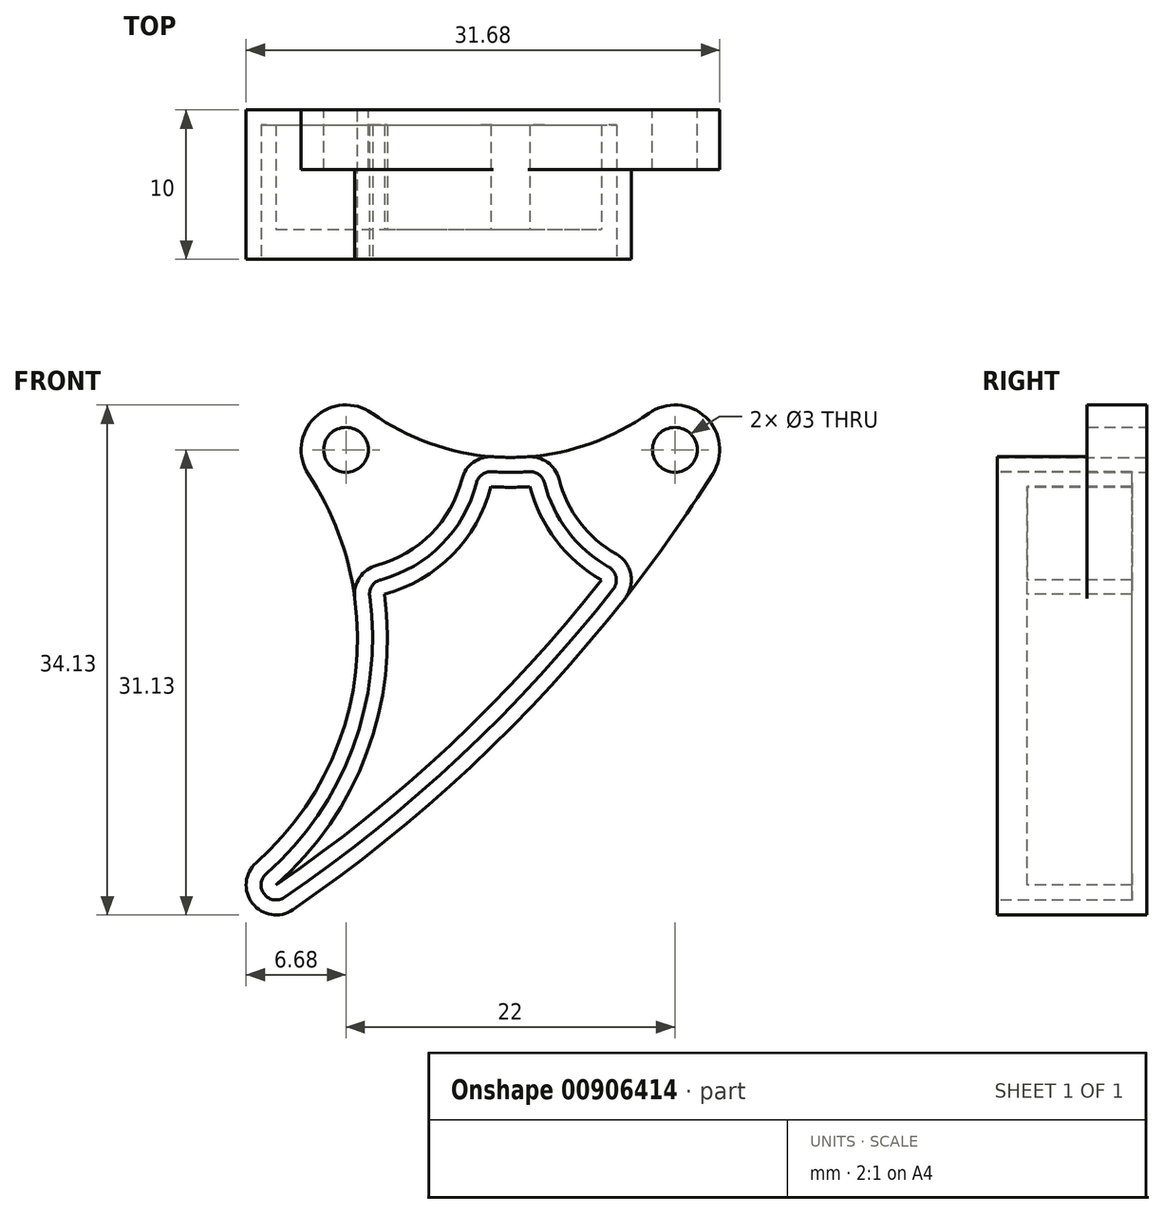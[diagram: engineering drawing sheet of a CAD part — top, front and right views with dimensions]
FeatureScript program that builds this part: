
annotation { "Feature Type Name" : "Feature", "Feature Type Description" : "" }
export const myFeature = defineFeature(function(context is Context, id is Id, definition is map)
    precondition{}
    {
        {
            var Q0;
            Q0=qCreatedBy(makeId("Front.planeOp"),FACE);
            var sketch = newSketch(context, id + "F0", { "sketchPlane" : qUnion([Q0])});
            skArc(sketch, "E0", {"start": v(1.74, 2.45) * mm, "mid": v(-2.08, 2.16) * mm, "end": v(-2.5, -1.65) * mm});
            skArc(sketch, "E1", {"start": v(24.54, -1.6) * mm, "mid": v(24.06, 2.18) * mm, "end": v(20.26, 2.45) * mm});
            skArc(sketch, "E2", {"start": v(1.74, 2.45) * mm, "mid": v(11, -0.5) * mm, "end": v(20.26, 2.45) * mm});
            skArc(sketch, "E3", {"start": v(-6, -27.63) * mm, "mid": v(0.6, -15.29) * mm, "end": v(-2.5, -1.65) * mm});
            skArc(sketch, "E4", {"start": v(-6, -27.63) * mm, "mid": v(-6.26, -30.35) * mm, "end": v(-3.55, -30.78) * mm});
            skArc(sketch, "E5", {"start": v(-3.55, -30.78) * mm, "mid": v(11.99, -17.62) * mm, "end": v(24.54, -1.6) * mm});
            skSolve(sketch);
        }
        {
            var Q0;
            Q0=makeQuery(id+"F0.imprint","IMPRINT",FACE,{"disambiguationData":[TD([[makeQuery(id+"F0.imprint","IMPRINT",EDGE,{"derivedFrom":sQuery(id+"F0.wireOp",EDGE,"E0")}),1.0]])]});
            extrude(context, id + "F1", {"entities" : qUnion([Q0]), "depth" : 4 * mm, "offsetDistance" : 25 * mm});
        }
        {
            var Q0;
            Q0=makeQuery(id+"F1.opExtrude","CAP_FACE",FACE,{"disambiguationData":[OSD([sQuery(id+"F0.wireOp",EDGE,"E0"),sQuery(id+"F0.wireOp",EDGE,"E1"),sQuery(id+"F0.wireOp",EDGE,"E2"),sQuery(id+"F0.wireOp",EDGE,"E3"),sQuery(id+"F0.wireOp",EDGE,"E4"),sQuery(id+"F0.wireOp",EDGE,"E5")])],"isStart":false});
            var sketch = newSketch(context, id + "F2", { "sketchPlane" : qUnion([Q0])});
            skArc(sketch, "E6", {"start": v(2.06, -7.73) * mm, "mid": v(5.69, -5.62) * mm, "end": v(7.75, -1.97) * mm});
            skArc(sketch, "E7", {"start": v(14.25, -1.97) * mm, "mid": v(15.65, -4.86) * mm, "end": v(18.07, -6.97) * mm});
            skArc(sketch, "E8.0", {"start": v(9.84, -0.47) * mm, "mid": v(11, -0.5) * mm, "end": v(12.16, -0.47) * mm});
            skArc(sketch, "E9.0", {"start": v(-6, -27.63) * mm, "mid": v(-0.49, -19.6) * mm, "end": v(0.6, -9.93) * mm});
            skArc(sketch, "E10.0", {"start": v(-6, -27.63) * mm, "mid": v(-6.26, -30.35) * mm, "end": v(-3.55, -30.78) * mm});
            skArc(sketch, "E11.0", {"start": v(-3.55, -30.78) * mm, "mid": v(8.35, -21.21) * mm, "end": v(18.66, -9.94) * mm});
            skPoint(sketch, "E12.newPointB", {"position": v(-2.5, -1.65) * mm});
            skArc(sketch, "E12.filletArc", {"start": v(2.06, -7.73) * mm, "mid": v(0.9, -8.55) * mm, "end": v(0.6, -9.93) * mm});
            skPoint(sketch, "E13.newPointB", {"position": v(1.74, 2.45) * mm});
            skArc(sketch, "E13.filletArc", {"start": v(9.84, -0.47) * mm, "mid": v(8.52, -0.84) * mm, "end": v(7.75, -1.97) * mm});
            skPoint(sketch, "E14.newPointA", {"position": v(20.26, 2.45) * mm});
            skArc(sketch, "E14.filletArc", {"start": v(14.25, -1.97) * mm, "mid": v(13.48, -0.84) * mm, "end": v(12.16, -0.47) * mm});
            skPoint(sketch, "E15.newPointB", {"position": v(24.54, -1.6) * mm});
            skArc(sketch, "E15.filletArc", {"start": v(18.66, -9.94) * mm, "mid": v(19.05, -8.32) * mm, "end": v(18.07, -6.97) * mm});
            skSolve(sketch);
        }
        {
            var Q0;
            Q0=makeQuery(id+"F2.imprint","IMPRINT",FACE,{"disambiguationData":[TD([[makeQuery(id+"F2.imprint","IMPRINT",EDGE,{"derivedFrom":sQuery(id+"F2.wireOp",EDGE,"E6")}),-1.0]])]});
            extrude(context, id + "F3", {"entities" : qUnion([Q0]), "operationType" : NewBodyOperationType.ADD, "depth" : 6 * mm, "offsetDistance" : 25 * mm});
        }
        {
            var Q0;
            Q0=makeQuery(id+"F3.opExtrude","CAP_FACE",FACE,{"disambiguationData":[OSD([sQuery(id+"F2.wireOp",EDGE,"E6"),sQuery(id+"F2.wireOp",EDGE,"E7"),sQuery(id+"F2.wireOp",EDGE,"E8.0"),sQuery(id+"F2.wireOp",EDGE,"E9.0"),sQuery(id+"F2.wireOp",EDGE,"E10.0"),sQuery(id+"F2.wireOp",EDGE,"E11.0"),sQuery(id+"F2.wireOp",EDGE,"E12.filletArc"),sQuery(id+"F2.wireOp",EDGE,"E13.filletArc"),sQuery(id+"F2.wireOp",EDGE,"E14.filletArc"),sQuery(id+"F2.wireOp",EDGE,"E15.filletArc")])],"isStart":false});
            var sketch = newSketch(context, id + "F4", { "sketchPlane" : qUnion([Q0])});
            skArc(sketch, "E16.0.0", {"start": v(-3.55, -30.78) * mm, "mid": v(8.35, -21.21) * mm, "end": v(18.66, -9.94) * mm});
            skArc(sketch, "E16.0.1", {"start": v(18.66, -9.94) * mm, "mid": v(19.05, -8.32) * mm, "end": v(18.07, -6.97) * mm});
            skArc(sketch, "E16.0.2", {"start": v(18.07, -6.97) * mm, "mid": v(15.65, -4.86) * mm, "end": v(14.25, -1.97) * mm});
            skArc(sketch, "E16.0.3", {"start": v(14.25, -1.97) * mm, "mid": v(13.48, -0.84) * mm, "end": v(12.16, -0.47) * mm});
            skArc(sketch, "E16.0.4", {"start": v(12.16, -0.47) * mm, "mid": v(11, -0.5) * mm, "end": v(9.84, -0.47) * mm});
            skArc(sketch, "E16.0.5", {"start": v(9.84, -0.47) * mm, "mid": v(8.52, -0.84) * mm, "end": v(7.75, -1.97) * mm});
            skArc(sketch, "E16.0.6", {"start": v(7.75, -1.97) * mm, "mid": v(5.69, -5.62) * mm, "end": v(2.06, -7.73) * mm});
            skArc(sketch, "E16.0.7", {"start": v(2.06, -7.73) * mm, "mid": v(0.9, -8.55) * mm, "end": v(0.6, -9.93) * mm});
            skArc(sketch, "E16.0.8", {"start": v(0.6, -9.93) * mm, "mid": v(-0.49, -19.6) * mm, "end": v(-6, -27.63) * mm});
            skArc(sketch, "E16.0.9", {"start": v(-6, -27.63) * mm, "mid": v(-6.26, -30.35) * mm, "end": v(-3.55, -30.78) * mm});
            skArc(sketch, "E17.0", {"start": v(-5.34, -28.38) * mm, "mid": v(-5.47, -29.74) * mm, "end": v(-4.12, -29.95) * mm});
            skArc(sketch, "E17.1", {"start": v(1.58, -9.8) * mm, "mid": v(0.45, -19.96) * mm, "end": v(-5.34, -28.38) * mm});
            skArc(sketch, "E17.2", {"start": v(-4.12, -29.95) * mm, "mid": v(7.67, -20.48) * mm, "end": v(17.87, -9.33) * mm});
            skArc(sketch, "E17.3", {"start": v(2.32, -8.7) * mm, "mid": v(1.74, -9.1) * mm, "end": v(1.58, -9.8) * mm});
            skArc(sketch, "E17.4", {"start": v(8.72, -2.21) * mm, "mid": v(6.4, -6.33) * mm, "end": v(2.32, -8.7) * mm});
            skArc(sketch, "E17.5", {"start": v(9.77, -1.46) * mm, "mid": v(9.1, -1.65) * mm, "end": v(8.72, -2.21) * mm});
            skArc(sketch, "E17.6", {"start": v(17.87, -9.33) * mm, "mid": v(18.07, -8.52) * mm, "end": v(17.58, -7.84) * mm});
            skArc(sketch, "E17.7", {"start": v(17.58, -7.84) * mm, "mid": v(14.85, -5.47) * mm, "end": v(13.28, -2.21) * mm});
            skArc(sketch, "E17.8", {"start": v(13.28, -2.21) * mm, "mid": v(12.9, -1.65) * mm, "end": v(12.23, -1.46) * mm});
            skArc(sketch, "E17.9", {"start": v(12.23, -1.46) * mm, "mid": v(11, -1.5) * mm, "end": v(9.77, -1.46) * mm});
            skSolve(sketch);
        }
        {
            var Q0;
            Q0=makeQuery(id+"F4.imprint","IMPRINT",FACE,{"disambiguationData":[TD([[makeQuery(id+"F4.imprint","IMPRINT",EDGE,{"derivedFrom":sQuery(id+"F4.wireOp",EDGE,"E17.0")}),1.0]])]});
            extrude(context, id + "F5", {"entities" : qUnion([Q0]), "operationType" : NewBodyOperationType.REMOVE, "oppositeDirection" : true, "depth" : 2 * mm, "offsetDistance" : 25 * mm});
        }
        {
            var Q0;
            Q0=makeQuery(id+"F5.boolean.opBoolean","COPY",FACE,{"derivedFrom":makeQuery(id+"F5.opExtrude","CAP_FACE",FACE,{"disambiguationData":[OSD([sQuery(id+"F4.wireOp",EDGE,"E17.0"),sQuery(id+"F4.wireOp",EDGE,"E17.1"),sQuery(id+"F4.wireOp",EDGE,"E17.2"),sQuery(id+"F4.wireOp",EDGE,"E17.3"),sQuery(id+"F4.wireOp",EDGE,"E17.4"),sQuery(id+"F4.wireOp",EDGE,"E17.5"),sQuery(id+"F4.wireOp",EDGE,"E17.6"),sQuery(id+"F4.wireOp",EDGE,"E17.7"),sQuery(id+"F4.wireOp",EDGE,"E17.8"),sQuery(id+"F4.wireOp",EDGE,"E17.9")])],"isStart":false})});
            var sketch = newSketch(context, id + "F6", { "sketchPlane" : qUnion([Q0])});
            skArc(sketch, "E18.0.0", {"start": v(13.28, -2.21) * mm, "mid": v(12.9, -1.65) * mm, "end": v(12.23, -1.46) * mm});
            skArc(sketch, "E18.0.1", {"start": v(12.23, -1.46) * mm, "mid": v(11, -1.5) * mm, "end": v(9.77, -1.46) * mm});
            skArc(sketch, "E18.0.2", {"start": v(9.77, -1.46) * mm, "mid": v(9.1, -1.65) * mm, "end": v(8.72, -2.21) * mm});
            skArc(sketch, "E18.0.3", {"start": v(8.72, -2.21) * mm, "mid": v(6.4, -6.33) * mm, "end": v(2.32, -8.7) * mm});
            skArc(sketch, "E18.0.4", {"start": v(2.32, -8.7) * mm, "mid": v(1.74, -9.1) * mm, "end": v(1.58, -9.8) * mm});
            skArc(sketch, "E18.0.5", {"start": v(1.58, -9.8) * mm, "mid": v(0.45, -19.96) * mm, "end": v(-5.34, -28.38) * mm});
            skArc(sketch, "E18.0.6", {"start": v(-5.34, -28.38) * mm, "mid": v(-5.47, -29.74) * mm, "end": v(-4.12, -29.95) * mm});
            skArc(sketch, "E18.0.7", {"start": v(-4.12, -29.95) * mm, "mid": v(7.67, -20.48) * mm, "end": v(17.87, -9.33) * mm});
            skArc(sketch, "E18.0.8", {"start": v(17.87, -9.33) * mm, "mid": v(18.07, -8.52) * mm, "end": v(17.58, -7.84) * mm});
            skArc(sketch, "E18.0.9", {"start": v(17.58, -7.84) * mm, "mid": v(14.85, -5.47) * mm, "end": v(13.28, -2.21) * mm});
            skArc(sketch, "E19.0", {"start": v(17.09, -8.71) * mm, "mid": v(14.06, -6.08) * mm, "end": v(12.3, -2.46) * mm});
            skLineSegment(sketch, "E19.1", {"start": v(17.09, -8.71) * mm, "end": v(17.09, -8.71) * mm});
            skLineSegment(sketch, "E19.2", {"start": v(12.3, -2.46) * mm, "end": v(12.3, -2.46) * mm});
            skArc(sketch, "E19.3", {"start": v(-4.68, -29.13) * mm, "mid": v(6.98, -19.75) * mm, "end": v(17.09, -8.71) * mm});
            skLineSegment(sketch, "E19.4", {"start": v(-4.68, -29.13) * mm, "end": v(-4.68, -29.13) * mm});
            skArc(sketch, "E19.5", {"start": v(2.57, -9.66) * mm, "mid": v(1.39, -20.3) * mm, "end": v(-4.68, -29.13) * mm});
            skArc(sketch, "E19.6", {"start": v(12.3, -2.46) * mm, "mid": v(11, -2.5) * mm, "end": v(9.7, -2.46) * mm});
            skLineSegment(sketch, "E19.7", {"start": v(9.7, -2.46) * mm, "end": v(9.7, -2.46) * mm});
            skArc(sketch, "E19.8", {"start": v(9.7, -2.46) * mm, "mid": v(7.11, -7.03) * mm, "end": v(2.57, -9.66) * mm});
            skLineSegment(sketch, "E19.9", {"start": v(2.57, -9.66) * mm, "end": v(2.57, -9.66) * mm});
            skSolve(sketch);
        }
        {
            var Q0;
            Q0=makeQuery(id+"F6.imprint","IMPRINT",FACE,{"disambiguationData":[TD([[makeQuery(id+"F6.imprint","IMPRINT",EDGE,{"derivedFrom":sQuery(id+"F6.wireOp",EDGE,"E19.0")}),1.0]])]});
            extrude(context, id + "F7", {"entities" : qUnion([Q0]), "operationType" : NewBodyOperationType.REMOVE, "oppositeDirection" : true, "depth" : 7 * mm, "offsetDistance" : 25 * mm});
        }
        {
            var Q0;
            Q0=qCreatedBy(makeId("Front.planeOp"),FACE);
            var sketch = newSketch(context, id + "F8", { "sketchPlane" : qUnion([Q0])});
            skCircle(sketch, "E20", {"center": v(0, 0) * mm, "radius": 1.5 * mm});
            skCircle(sketch, "E21", {"center": v(22, 0) * mm, "radius": 1.5 * mm});
            skSolve(sketch);
        }
        {
            var Q0;
            Q0=qSketchRegion(id+"F8",true);
            extrude(context, id + "F9", {"entities" : qUnion([Q0]), "operationType" : NewBodyOperationType.REMOVE, "endBound" : BoundingType.THROUGH_ALL, "depth" : 25 * mm, "offsetDistance" : 25 * mm});
        }
    });
